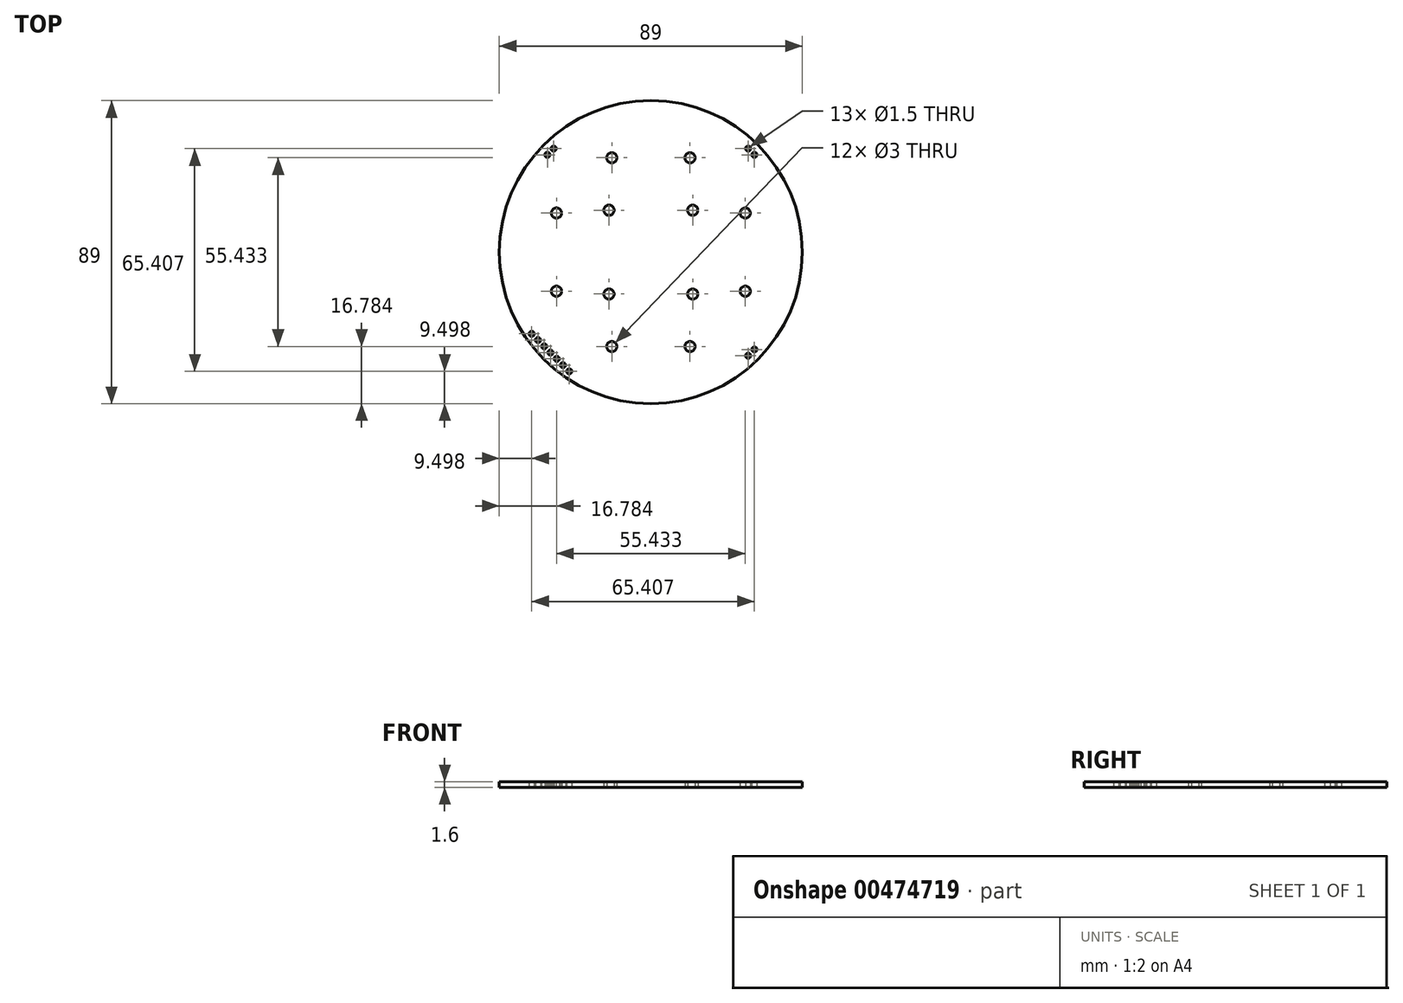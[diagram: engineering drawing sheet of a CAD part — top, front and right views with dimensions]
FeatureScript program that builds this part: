
annotation { "Feature Type Name" : "Feature", "Feature Type Description" : "" }
export const myFeature = defineFeature(function(context is Context, id is Id, definition is map)
    precondition{}
    {
        {
            var Q0;
            Q0=qCreatedBy(makeId("Top.planeOp"),FACE);
            var sketch = newSketch(context, id + "F0", { "sketchPlane" : qUnion([Q0])});
            skCircle(sketch, "E0", {"center": v(0, 0) * mm, "radius": 44.5 * mm});
            skLineSegment(sketch, "E1.bottom", {"start": v(-12.3, 12.3) * mm, "end": v(12.3, 12.3) * mm, "construction": true});
            skLineSegment(sketch, "E1.top", {"start": v(-12.3, -12.3) * mm, "end": v(12.3, -12.3) * mm, "construction": true});
            skLineSegment(sketch, "E1.left", {"start": v(-12.3, 12.3) * mm, "end": v(-12.3, -12.3) * mm, "construction": true});
            skLineSegment(sketch, "E1.right", {"start": v(12.3, 12.3) * mm, "end": v(12.3, -12.3) * mm, "construction": true});
            skCircle(sketch, "E2", {"center": v(-12.3, 12.3) * mm, "radius": 1.5 * mm});
            skCircle(sketch, "E3", {"center": v(12.3, 12.3) * mm, "radius": 1.5 * mm});
            skCircle(sketch, "E4", {"center": v(-12.3, -12.3) * mm, "radius": 1.5 * mm});
            skCircle(sketch, "E5", {"center": v(12.3, -12.3) * mm, "radius": 1.5 * mm});
            skLineSegment(sketch, "E6", {"start": v(-41.11, 17.03) * mm, "end": v(41.11, -17.03) * mm, "construction": true});
            skLineSegment(sketch, "E7", {"start": v(-41.11, -17.03) * mm, "end": v(41.11, 17.03) * mm, "construction": true});
            skLineSegment(sketch, "E8", {"start": v(-17.03, 41.11) * mm, "end": v(17.03, -41.11) * mm, "construction": true});
            skLineSegment(sketch, "E9", {"start": v(-17.03, -41.11) * mm, "end": v(17.03, 41.11) * mm, "construction": true});
            skCircle(sketch, "E10", {"center": v(0, 0) * mm, "radius": 30 * mm, "construction": true});
            skCircle(sketch, "E11", {"center": v(-11.48, 27.72) * mm, "radius": 1.5 * mm});
            skCircle(sketch, "E12", {"center": v(11.48, 27.72) * mm, "radius": 1.5 * mm});
            skCircle(sketch, "E13", {"center": v(27.72, 11.48) * mm, "radius": 1.5 * mm});
            skCircle(sketch, "E14", {"center": v(27.72, -11.48) * mm, "radius": 1.5 * mm});
            skCircle(sketch, "E15", {"center": v(11.48, -27.72) * mm, "radius": 1.5 * mm});
            skCircle(sketch, "E16", {"center": v(-11.48, -27.72) * mm, "radius": 1.5 * mm});
            skCircle(sketch, "E17", {"center": v(-27.72, -11.48) * mm, "radius": 1.5 * mm});
            skCircle(sketch, "E18", {"center": v(-27.72, 11.48) * mm, "radius": 1.5 * mm});
            skLineSegment(sketch, "E19", {"start": v(-31.47, 31.47) * mm, "end": v(31.47, -31.47) * mm, "construction": true});
            skLineSegment(sketch, "E20", {"start": v(-31.47, -31.47) * mm, "end": v(31.47, 31.47) * mm, "construction": true});
            skLineSegment(sketch, "E21", {"start": v(-36.84, -23.97) * mm, "end": v(-23.97, -36.84) * mm, "construction": true});
            skLineSegment(sketch, "E22", {"start": v(-23.97, -36.84) * mm, "end": v(-22.13, -35) * mm, "construction": true});
            skLineSegment(sketch, "E23", {"start": v(-22.13, -35) * mm, "end": v(-35, -22.13) * mm, "construction": true});
            skLineSegment(sketch, "E24", {"start": v(-35, -22.13) * mm, "end": v(-36.84, -23.97) * mm, "construction": true});
            skLineSegment(sketch, "E25", {"start": v(26.73, -30.4) * mm, "end": v(28.57, -32.24) * mm, "construction": true});
            skLineSegment(sketch, "E26", {"start": v(28.57, -32.24) * mm, "end": v(32.24, -28.57) * mm, "construction": true});
            skLineSegment(sketch, "E27", {"start": v(32.24, -28.57) * mm, "end": v(30.4, -26.73) * mm, "construction": true});
            skLineSegment(sketch, "E28", {"start": v(30.4, -26.73) * mm, "end": v(26.73, -30.4) * mm, "construction": true});
            skLineSegment(sketch, "E29", {"start": v(30.4, 26.73) * mm, "end": v(32.24, 28.57) * mm, "construction": true});
            skLineSegment(sketch, "E30", {"start": v(32.24, 28.57) * mm, "end": v(28.57, 32.24) * mm, "construction": true});
            skLineSegment(sketch, "E31", {"start": v(28.57, 32.24) * mm, "end": v(26.73, 30.4) * mm, "construction": true});
            skLineSegment(sketch, "E32", {"start": v(26.73, 30.4) * mm, "end": v(30.4, 26.73) * mm, "construction": true});
            skLineSegment(sketch, "E33", {"start": v(-32.24, 28.57) * mm, "end": v(-30.4, 26.73) * mm, "construction": true});
            skLineSegment(sketch, "E34", {"start": v(-30.4, 26.73) * mm, "end": v(-26.73, 30.4) * mm, "construction": true});
            skLineSegment(sketch, "E35", {"start": v(-26.73, 30.4) * mm, "end": v(-28.57, 32.24) * mm, "construction": true});
            skLineSegment(sketch, "E36", {"start": v(-28.57, 32.24) * mm, "end": v(-32.24, 28.57) * mm, "construction": true});
            skCircle(sketch, "E37", {"center": v(-28.57, 30.4) * mm, "radius": 0.75 * mm});
            skCircle(sketch, "E38", {"center": v(-30.4, 28.57) * mm, "radius": 0.75 * mm});
            skCircle(sketch, "E39", {"center": v(28.57, 30.4) * mm, "radius": 0.75 * mm});
            skCircle(sketch, "E40", {"center": v(30.4, 28.57) * mm, "radius": 0.75 * mm});
            skCircle(sketch, "E41", {"center": v(28.57, -30.4) * mm, "radius": 0.75 * mm});
            skCircle(sketch, "E42", {"center": v(30.4, -28.57) * mm, "radius": 0.75 * mm});
            skCircle(sketch, "E43", {"center": v(-35, -23.97) * mm, "radius": 0.75 * mm});
            skCircle(sketch, "E44", {"center": v(-33.16, -25.8) * mm, "radius": 0.75 * mm});
            skCircle(sketch, "E45", {"center": v(-31.32, -27.65) * mm, "radius": 0.75 * mm});
            skCircle(sketch, "E46", {"center": v(-29.49, -29.49) * mm, "radius": 0.75 * mm});
            skCircle(sketch, "E47", {"center": v(-27.65, -31.32) * mm, "radius": 0.75 * mm});
            skCircle(sketch, "E48", {"center": v(-25.8, -33.16) * mm, "radius": 0.75 * mm});
            skCircle(sketch, "E49", {"center": v(-23.97, -35) * mm, "radius": 0.75 * mm});
            skLineSegment(sketch, "E50", {"start": v(-35.92, -23.05) * mm, "end": v(-23.05, -35.92) * mm, "construction": true});
            skSolve(sketch);
        }
        {
            var Q0;
            Q0 = qSketchRegion(id + "F0", true);
            extrude(context, id + "F1", {"entities" : qUnion([Q0]), "depth" : 1.6 * mm});
        }
    });
